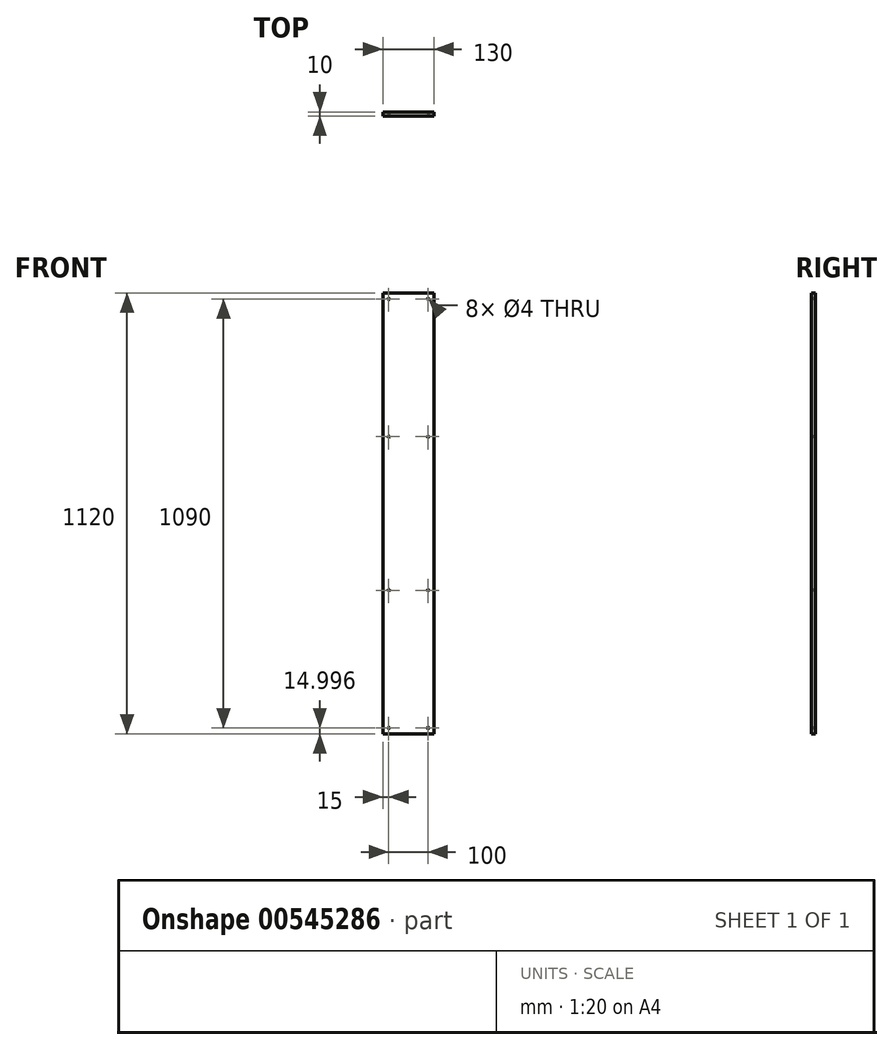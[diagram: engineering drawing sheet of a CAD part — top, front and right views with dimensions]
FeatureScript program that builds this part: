
annotation { "Feature Type Name" : "Feature", "Feature Type Description" : "" }
export const myFeature = defineFeature(function(context is Context, id is Id, definition is map)
    precondition{}
    {
        {
            var Q0;
            Q0=qCreatedBy(makeId("Front.planeOp"),FACE);
            var sketch = newSketch(context, id + "F0", { "sketchPlane" : qUnion([Q0])});
            skLineSegment(sketch, "E0.bottom", {"start": v(-242.64, 570.38) * mm, "end": v(-112.64, 570.38) * mm});
            skLineSegment(sketch, "E0.top", {"start": v(-242.64, -549.62) * mm, "end": v(-112.64, -549.62) * mm});
            skLineSegment(sketch, "E0.left", {"start": v(-242.64, 570.38) * mm, "end": v(-242.64, -549.62) * mm});
            skLineSegment(sketch, "E0.right", {"start": v(-112.64, 570.38) * mm, "end": v(-112.64, -549.62) * mm});
            skSolve(sketch);
        }
        {
            var Q0;
            Q0=makeQuery(id+"F0.imprint","IMPRINT",FACE,{"disambiguationData":[TD([[makeQuery(id+"F0.imprint","IMPRINT",EDGE,{"derivedFrom":sQuery(id+"F0.wireOp",EDGE,"E0.bottom")}),-1.0]])]});
            extrude(context, id + "F1", {"entities" : qUnion([Q0]), "depth" : 10 * mm, "offsetDistance" : 25 * mm});
        }
        {
            var Q0;
            Q0=makeQuery(id+"F1.opExtrude","CAP_FACE",FACE,{"disambiguationData":[OSD([sQuery(id+"F0.wireOp",EDGE,"E0.bottom"),sQuery(id+"F0.wireOp",EDGE,"E0.top"),sQuery(id+"F0.wireOp",EDGE,"E0.left"),sQuery(id+"F0.wireOp",EDGE,"E0.right")])],"isStart":false});
            var sketch = newSketch(context, id + "F2", { "sketchPlane" : qUnion([Q0])});
            skPoint(sketch, "E1", {"position": v(-227.64, 555.38) * mm});
            skPoint(sketch, "E2", {"position": v(-127.64, 555.38) * mm});
            skLineSegment(sketch, "E3.bottom", {"start": v(-227.64, 555.38) * mm, "end": v(-127.64, 555.38) * mm, "construction": true});
            skLineSegment(sketch, "E3.top", {"start": v(-227.64, -534.62) * mm, "end": v(-127.64, -534.62) * mm, "construction": true});
            skLineSegment(sketch, "E3.left", {"start": v(-227.64, 555.38) * mm, "end": v(-227.64, -534.62) * mm, "construction": true});
            skLineSegment(sketch, "E3.right", {"start": v(-127.64, 555.38) * mm, "end": v(-127.64, -534.62) * mm, "construction": true});
            skPoint(sketch, "E4", {"position": v(-227.64, -534.62) * mm});
            skPoint(sketch, "E5", {"position": v(-127.64, -534.62) * mm});
            skPoint(sketch, "E6", {"position": v(-227.64, -184.62) * mm});
            skPoint(sketch, "E7", {"position": v(-227.64, 205.38) * mm});
            skPoint(sketch, "E8", {"position": v(-127.64, 205.38) * mm});
            skPoint(sketch, "E9", {"position": v(-127.64, -184.62) * mm});
            skLineSegment(sketch, "E10", {"start": v(-227.64, 205.38) * mm, "end": v(-127.64, 205.38) * mm, "construction": true});
            skLineSegment(sketch, "E11", {"start": v(-227.64, -184.62) * mm, "end": v(-127.64, -184.62) * mm, "construction": true});
            skSolve(sketch);
        }
        {
            var Q0;
            Q0=sQuery(id+"F2.wireOp",VERTEX,"E1");
            var Q1;
            Q1=sQuery(id+"F2.wireOp",VERTEX,"E2");
            var Q2;
            Q2=sQuery(id+"F2.wireOp",VERTEX,"E5");
            var Q3;
            Q3=sQuery(id+"F2.wireOp",VERTEX,"E4");
            var Q4;
            Q4=sQuery(id+"F2.wireOp",VERTEX,"E7");
            var Q5;
            Q5=sQuery(id+"F2.wireOp",VERTEX,"E8");
            var Q6;
            Q6=sQuery(id+"F2.wireOp",VERTEX,"E9");
            var Q7;
            Q7=sQuery(id+"F2.wireOp",VERTEX,"E6");
            var Q8;
            Q8=makeQuery(id+"F1.opExtrude","SWEPT_BODY",BODY,{"disambiguationData":[OSD([sQuery(id+"F0.wireOp",EDGE,"E0.bottom"),sQuery(id+"F0.wireOp",EDGE,"E0.top"),sQuery(id+"F0.wireOp",EDGE,"E0.left"),sQuery(id+"F0.wireOp",EDGE,"E0.right")])]});
            hole(context, id + "F3", {"style" : HoleStyle.SIMPLE, "endStyle" : HoleEndStyle.THROUGH, "holeDiameter" : 4 * mm, "isTappedThrough" : true, "tappedDepth" : 12 * mm, "tapClearance" : 3, "startFromSketch" : true, "locations" : qUnion([Q0, Q1, Q2, Q3, Q4, Q5, Q6, Q7]), "scope" : qUnion([Q8])});
        }
    });
